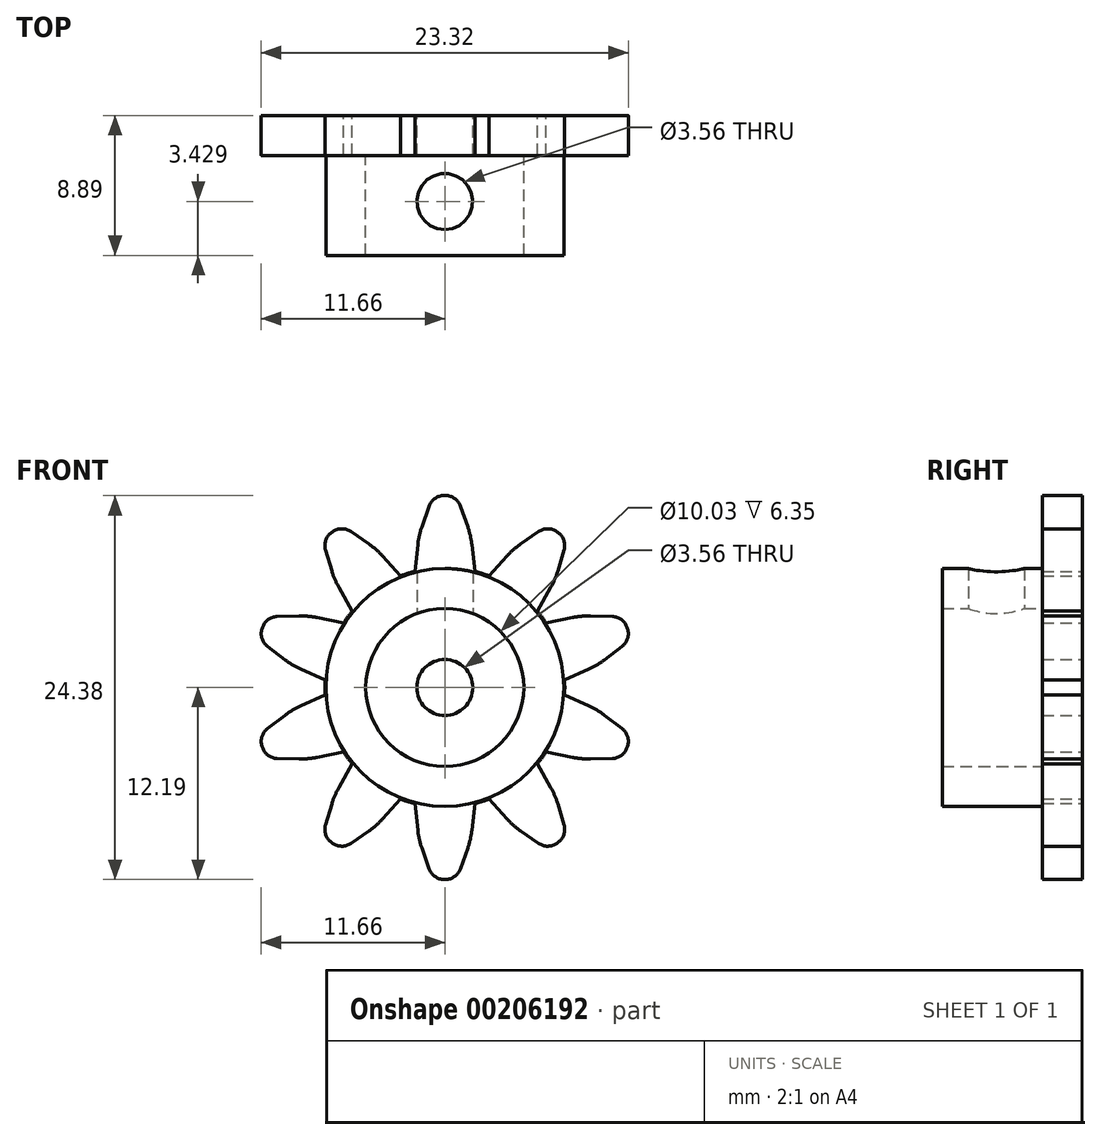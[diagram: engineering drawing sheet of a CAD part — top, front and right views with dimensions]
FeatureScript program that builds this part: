
annotation { "Feature Type Name" : "Feature", "Feature Type Description" : "" }
export const myFeature = defineFeature(function(context is Context, id is Id, definition is map)
    precondition{}
    {
        {
            var Q0;
            Q0=qCreatedBy(makeId("Front.planeOp"),FACE);
            var sketch = newSketch(context, id + "F0", { "sketchPlane" : qUnion([Q0])});
            skCircle(sketch, "E0", {"center": v(0, 0) * mm, "radius": 7.62 * mm});
            skLineSegment(sketch, "E1", {"start": v(-1.9, 7.38) * mm, "end": v(-0.76, 12.2) * mm, "construction": true});
            skLineSegment(sketch, "E2", {"start": v(-0.76, 12.2) * mm, "end": v(0.76, 12.2) * mm});
            skLineSegment(sketch, "E3", {"start": v(0.76, 12.2) * mm, "end": v(1.9, 7.38) * mm, "construction": true});
            skLineSegment(sketch, "E4", {"start": v(-1.9, 7.38) * mm, "end": v(-1.65, 9.65) * mm});
            skPoint(sketch, "E4.endSnap0", {"position": v(-1.33, 9.79) * mm});
            skLineSegment(sketch, "E5", {"start": v(-1.65, 9.65) * mm, "end": v(-0.76, 12.2) * mm});
            skLineSegment(sketch, "E6", {"start": v(1.9, 7.38) * mm, "end": v(1.65, 9.65) * mm});
            skPoint(sketch, "E6.endSnap0", {"position": v(1.33, 9.79) * mm});
            skLineSegment(sketch, "E7", {"start": v(1.65, 9.65) * mm, "end": v(0.76, 12.2) * mm});
            skLineSegment(sketch, "E8.1.0", {"start": v(-7.78, 9.42) * mm, "end": v(-6.55, 10.31) * mm});
            skLineSegment(sketch, "E8.1.1", {"start": v(-4.34, 8.78) * mm, "end": v(-6.55, 10.31) * mm});
            skLineSegment(sketch, "E8.1.2", {"start": v(-2.8, 7.09) * mm, "end": v(-4.34, 8.78) * mm});
            skLineSegment(sketch, "E8.1.3", {"start": v(-7, 6.84) * mm, "end": v(-7.78, 9.42) * mm});
            skLineSegment(sketch, "E8.1.4", {"start": v(-5.88, 4.85) * mm, "end": v(-7, 6.84) * mm});
            skLineSegment(sketch, "E8.2.0", {"start": v(-11.83, 3.04) * mm, "end": v(-11.36, 4.5) * mm});
            skLineSegment(sketch, "E8.2.1", {"start": v(-8.67, 4.55) * mm, "end": v(-11.36, 4.5) * mm});
            skLineSegment(sketch, "E8.2.2", {"start": v(-6.43, 4.1) * mm, "end": v(-8.67, 4.55) * mm});
            skLineSegment(sketch, "E8.2.3", {"start": v(-9.69, 1.41) * mm, "end": v(-11.83, 3.04) * mm});
            skLineSegment(sketch, "E8.2.4", {"start": v(-7.6, 0.47) * mm, "end": v(-9.69, 1.41) * mm});
            skLineSegment(sketch, "E8.3.0", {"start": v(-11.36, -4.5) * mm, "end": v(-11.83, -3.04) * mm});
            skLineSegment(sketch, "E8.3.1", {"start": v(-9.69, -1.41) * mm, "end": v(-11.83, -3.04) * mm});
            skLineSegment(sketch, "E8.3.2", {"start": v(-7.6, -0.47) * mm, "end": v(-9.69, -1.41) * mm});
            skLineSegment(sketch, "E8.3.3", {"start": v(-8.67, -4.55) * mm, "end": v(-11.36, -4.5) * mm});
            skLineSegment(sketch, "E8.3.4", {"start": v(-6.43, -4.1) * mm, "end": v(-8.67, -4.55) * mm});
            skLineSegment(sketch, "E8.4.0", {"start": v(-6.55, -10.31) * mm, "end": v(-7.78, -9.42) * mm});
            skLineSegment(sketch, "E8.4.1", {"start": v(-7, -6.84) * mm, "end": v(-7.78, -9.42) * mm});
            skLineSegment(sketch, "E8.4.2", {"start": v(-5.88, -4.85) * mm, "end": v(-7, -6.84) * mm});
            skLineSegment(sketch, "E8.4.3", {"start": v(-4.34, -8.78) * mm, "end": v(-6.55, -10.31) * mm});
            skLineSegment(sketch, "E8.4.4", {"start": v(-2.8, -7.09) * mm, "end": v(-4.34, -8.78) * mm});
            skLineSegment(sketch, "E8.5.0", {"start": v(0.76, -12.2) * mm, "end": v(-0.76, -12.2) * mm});
            skLineSegment(sketch, "E8.5.1", {"start": v(-1.65, -9.65) * mm, "end": v(-0.76, -12.2) * mm});
            skLineSegment(sketch, "E8.5.2", {"start": v(-1.9, -7.38) * mm, "end": v(-1.65, -9.65) * mm});
            skLineSegment(sketch, "E8.5.3", {"start": v(1.65, -9.65) * mm, "end": v(0.76, -12.2) * mm});
            skLineSegment(sketch, "E8.5.4", {"start": v(1.9, -7.38) * mm, "end": v(1.65, -9.65) * mm});
            skLineSegment(sketch, "E8.6.0", {"start": v(7.78, -9.42) * mm, "end": v(6.55, -10.31) * mm});
            skLineSegment(sketch, "E8.6.1", {"start": v(4.34, -8.78) * mm, "end": v(6.55, -10.31) * mm});
            skLineSegment(sketch, "E8.6.2", {"start": v(2.8, -7.09) * mm, "end": v(4.34, -8.78) * mm});
            skLineSegment(sketch, "E8.6.3", {"start": v(7, -6.84) * mm, "end": v(7.78, -9.42) * mm});
            skLineSegment(sketch, "E8.6.4", {"start": v(5.88, -4.85) * mm, "end": v(7, -6.84) * mm});
            skLineSegment(sketch, "E8.7.0", {"start": v(11.83, -3.04) * mm, "end": v(11.36, -4.5) * mm});
            skLineSegment(sketch, "E8.7.1", {"start": v(8.67, -4.55) * mm, "end": v(11.36, -4.5) * mm});
            skLineSegment(sketch, "E8.7.2", {"start": v(6.43, -4.1) * mm, "end": v(8.67, -4.55) * mm});
            skLineSegment(sketch, "E8.7.3", {"start": v(9.69, -1.41) * mm, "end": v(11.83, -3.04) * mm});
            skLineSegment(sketch, "E8.7.4", {"start": v(7.6, -0.47) * mm, "end": v(9.69, -1.41) * mm});
            skLineSegment(sketch, "E8.8.0", {"start": v(11.36, 4.5) * mm, "end": v(11.83, 3.04) * mm});
            skLineSegment(sketch, "E8.8.1", {"start": v(9.69, 1.41) * mm, "end": v(11.83, 3.04) * mm});
            skLineSegment(sketch, "E8.8.2", {"start": v(7.6, 0.47) * mm, "end": v(9.69, 1.41) * mm});
            skLineSegment(sketch, "E8.8.3", {"start": v(8.67, 4.55) * mm, "end": v(11.36, 4.5) * mm});
            skLineSegment(sketch, "E8.8.4", {"start": v(6.43, 4.1) * mm, "end": v(8.67, 4.55) * mm});
            skLineSegment(sketch, "E8.9.0", {"start": v(6.55, 10.31) * mm, "end": v(7.78, 9.42) * mm});
            skLineSegment(sketch, "E8.9.1", {"start": v(7, 6.84) * mm, "end": v(7.78, 9.42) * mm});
            skLineSegment(sketch, "E8.9.2", {"start": v(5.88, 4.85) * mm, "end": v(7, 6.84) * mm});
            skLineSegment(sketch, "E8.9.3", {"start": v(4.34, 8.78) * mm, "end": v(6.55, 10.31) * mm});
            skLineSegment(sketch, "E8.9.4", {"start": v(2.8, 7.09) * mm, "end": v(4.34, 8.78) * mm});
            skCircle(sketch, "E9", {"center": v(0, 0) * mm, "radius": 1.78 * mm});
            skSolve(sketch);
        }
        {
            var Q0;
            Q0=qSketchRegion(id+"F0",true);
            extrude(context, id + "F1", {"entities" : qUnion([Q0]), "depth" : 2.54 * mm});
        }
        {
            var Q0;
            Q0=makeQuery(id+"F1.opExtrude","CAP_FACE",FACE,{"disambiguationData":[OSD([sQuery(id+"F0.wireOp",EDGE,"E0"),sQuery(id+"F0.wireOp",EDGE,"E2"),sQuery(id+"F0.wireOp",EDGE,"E4"),sQuery(id+"F0.wireOp",EDGE,"E5"),sQuery(id+"F0.wireOp",EDGE,"E6"),sQuery(id+"F0.wireOp",EDGE,"E7"),sQuery(id+"F0.wireOp",EDGE,"E8.1.0"),sQuery(id+"F0.wireOp",EDGE,"E8.1.1"),sQuery(id+"F0.wireOp",EDGE,"E8.1.2"),sQuery(id+"F0.wireOp",EDGE,"E8.1.3"),sQuery(id+"F0.wireOp",EDGE,"E8.1.4"),sQuery(id+"F0.wireOp",EDGE,"E8.2.0"),sQuery(id+"F0.wireOp",EDGE,"E8.2.1"),sQuery(id+"F0.wireOp",EDGE,"E8.2.2"),sQuery(id+"F0.wireOp",EDGE,"E8.2.3"),sQuery(id+"F0.wireOp",EDGE,"E8.2.4"),sQuery(id+"F0.wireOp",EDGE,"E8.3.0"),sQuery(id+"F0.wireOp",EDGE,"E8.3.1"),sQuery(id+"F0.wireOp",EDGE,"E8.3.2"),sQuery(id+"F0.wireOp",EDGE,"E8.3.3"),sQuery(id+"F0.wireOp",EDGE,"E8.3.4"),sQuery(id+"F0.wireOp",EDGE,"E8.4.0"),sQuery(id+"F0.wireOp",EDGE,"E8.4.1"),sQuery(id+"F0.wireOp",EDGE,"E8.4.2"),sQuery(id+"F0.wireOp",EDGE,"E8.4.3"),sQuery(id+"F0.wireOp",EDGE,"E8.4.4"),sQuery(id+"F0.wireOp",EDGE,"E8.5.0"),sQuery(id+"F0.wireOp",EDGE,"E8.5.1"),sQuery(id+"F0.wireOp",EDGE,"E8.5.2"),sQuery(id+"F0.wireOp",EDGE,"E8.5.3"),sQuery(id+"F0.wireOp",EDGE,"E8.5.4"),sQuery(id+"F0.wireOp",EDGE,"E8.6.0"),sQuery(id+"F0.wireOp",EDGE,"E8.6.1"),sQuery(id+"F0.wireOp",EDGE,"E8.6.2"),sQuery(id+"F0.wireOp",EDGE,"E8.6.3"),sQuery(id+"F0.wireOp",EDGE,"E8.6.4"),sQuery(id+"F0.wireOp",EDGE,"E8.7.0"),sQuery(id+"F0.wireOp",EDGE,"E8.7.1"),sQuery(id+"F0.wireOp",EDGE,"E8.7.2"),sQuery(id+"F0.wireOp",EDGE,"E8.7.3"),sQuery(id+"F0.wireOp",EDGE,"E8.7.4"),sQuery(id+"F0.wireOp",EDGE,"E8.8.0"),sQuery(id+"F0.wireOp",EDGE,"E8.8.1"),sQuery(id+"F0.wireOp",EDGE,"E8.8.2"),sQuery(id+"F0.wireOp",EDGE,"E8.8.3"),sQuery(id+"F0.wireOp",EDGE,"E8.8.4"),sQuery(id+"F0.wireOp",EDGE,"E8.9.0"),sQuery(id+"F0.wireOp",EDGE,"E8.9.1"),sQuery(id+"F0.wireOp",EDGE,"E8.9.2"),sQuery(id+"F0.wireOp",EDGE,"E8.9.3"),sQuery(id+"F0.wireOp",EDGE,"E8.9.4"),sQuery(id+"F0.wireOp",EDGE,"E9")])],"isStart":false});
            var sketch = newSketch(context, id + "F2", { "sketchPlane" : qUnion([Q0])});
            skCircle(sketch, "E10", {"center": v(0, 0) * mm, "radius": 7.56 * mm});
            skCircle(sketch, "E11", {"center": v(0, 0) * mm, "radius": 5.02 * mm});
            skSolve(sketch);
        }
        {
            var Q0;
            Q0=qSketchRegion(id+"F2",true);
            extrude(context, id + "F3", {"entities" : qUnion([Q0]), "operationType" : NewBodyOperationType.ADD, "depth" : 6.35 * mm});
        }
        {
            var Q0;
            Q0=makeQuery(id+"F1.opExtrude","SWEPT_EDGE",EDGE,{"disambiguationData":[OSD([sQuery(id+"F0.wireOp",EDGE,"E8.9.1"),sQuery(id+"F0.wireOp",EDGE,"E8.9.2")])]});
            var Q1;
            Q1=makeQuery(id+"F1.opExtrude","SWEPT_EDGE",EDGE,{"disambiguationData":[OSD([sQuery(id+"F0.wireOp",EDGE,"E8.9.3"),sQuery(id+"F0.wireOp",EDGE,"E8.9.4")])]});
            var Q2;
            Q2=makeQuery(id+"F1.opExtrude","SWEPT_EDGE",EDGE,{"disambiguationData":[OSD([sQuery(id+"F0.wireOp",EDGE,"E6"),sQuery(id+"F0.wireOp",EDGE,"E7")])]});
            var Q3;
            Q3=makeQuery(id+"F1.opExtrude","SWEPT_EDGE",EDGE,{"disambiguationData":[OSD([sQuery(id+"F0.wireOp",EDGE,"E8.1.1"),sQuery(id+"F0.wireOp",EDGE,"E8.1.2")])]});
            var Q4;
            Q4=makeQuery(id+"F1.opExtrude","SWEPT_EDGE",EDGE,{"disambiguationData":[OSD([sQuery(id+"F0.wireOp",EDGE,"E8.2.1"),sQuery(id+"F0.wireOp",EDGE,"E8.2.2")])]});
            var Q5;
            Q5=makeQuery(id+"F1.opExtrude","SWEPT_EDGE",EDGE,{"disambiguationData":[OSD([sQuery(id+"F0.wireOp",EDGE,"E8.3.1"),sQuery(id+"F0.wireOp",EDGE,"E8.3.2")])]});
            var Q6;
            Q6=makeQuery(id+"F1.opExtrude","SWEPT_EDGE",EDGE,{"disambiguationData":[OSD([sQuery(id+"F0.wireOp",EDGE,"E8.4.1"),sQuery(id+"F0.wireOp",EDGE,"E8.4.2")])]});
            var Q7;
            Q7=makeQuery(id+"F1.opExtrude","SWEPT_EDGE",EDGE,{"disambiguationData":[OSD([sQuery(id+"F0.wireOp",EDGE,"E8.5.1"),sQuery(id+"F0.wireOp",EDGE,"E8.5.2")])]});
            var Q8;
            Q8=makeQuery(id+"F1.opExtrude","SWEPT_EDGE",EDGE,{"disambiguationData":[OSD([sQuery(id+"F0.wireOp",EDGE,"E8.6.1"),sQuery(id+"F0.wireOp",EDGE,"E8.6.2")])]});
            var Q9;
            Q9=makeQuery(id+"F1.opExtrude","SWEPT_EDGE",EDGE,{"disambiguationData":[OSD([sQuery(id+"F0.wireOp",EDGE,"E8.7.1"),sQuery(id+"F0.wireOp",EDGE,"E8.7.2")])]});
            var Q10;
            Q10=makeQuery(id+"F1.opExtrude","SWEPT_EDGE",EDGE,{"disambiguationData":[OSD([sQuery(id+"F0.wireOp",EDGE,"E8.8.1"),sQuery(id+"F0.wireOp",EDGE,"E8.8.2")])]});
            var Q11;
            Q11=makeQuery(id+"F1.opExtrude","SWEPT_EDGE",EDGE,{"disambiguationData":[OSD([sQuery(id+"F0.wireOp",EDGE,"E8.7.3"),sQuery(id+"F0.wireOp",EDGE,"E8.7.4")])]});
            var Q12;
            Q12=makeQuery(id+"F1.opExtrude","SWEPT_EDGE",EDGE,{"disambiguationData":[OSD([sQuery(id+"F0.wireOp",EDGE,"E8.8.3"),sQuery(id+"F0.wireOp",EDGE,"E8.8.4")])]});
            var Q13;
            Q13=makeQuery(id+"F1.opExtrude","SWEPT_EDGE",EDGE,{"disambiguationData":[OSD([sQuery(id+"F0.wireOp",EDGE,"E4"),sQuery(id+"F0.wireOp",EDGE,"E5")])]});
            var Q14;
            Q14=makeQuery(id+"F1.opExtrude","SWEPT_EDGE",EDGE,{"disambiguationData":[OSD([sQuery(id+"F0.wireOp",EDGE,"E8.1.3"),sQuery(id+"F0.wireOp",EDGE,"E8.1.4")])]});
            var Q15;
            Q15=makeQuery(id+"F1.opExtrude","SWEPT_EDGE",EDGE,{"disambiguationData":[OSD([sQuery(id+"F0.wireOp",EDGE,"E8.2.3"),sQuery(id+"F0.wireOp",EDGE,"E8.2.4")])]});
            var Q16;
            Q16=makeQuery(id+"F1.opExtrude","SWEPT_EDGE",EDGE,{"disambiguationData":[OSD([sQuery(id+"F0.wireOp",EDGE,"E8.3.3"),sQuery(id+"F0.wireOp",EDGE,"E8.3.4")])]});
            var Q17;
            Q17=makeQuery(id+"F1.opExtrude","SWEPT_EDGE",EDGE,{"disambiguationData":[OSD([sQuery(id+"F0.wireOp",EDGE,"E8.4.3"),sQuery(id+"F0.wireOp",EDGE,"E8.4.4")])]});
            var Q18;
            Q18=makeQuery(id+"F1.opExtrude","SWEPT_EDGE",EDGE,{"disambiguationData":[OSD([sQuery(id+"F0.wireOp",EDGE,"E8.5.3"),sQuery(id+"F0.wireOp",EDGE,"E8.5.4")])]});
            var Q19;
            Q19=makeQuery(id+"F1.opExtrude","SWEPT_EDGE",EDGE,{"disambiguationData":[OSD([sQuery(id+"F0.wireOp",EDGE,"E8.6.3"),sQuery(id+"F0.wireOp",EDGE,"E8.6.4")])]});
            fillet(context, id + "F4", {"entities" : qUnion([Q0, Q1, Q2, Q3, Q4, Q5, Q6, Q7, Q8, Q9, Q10, Q11, Q12, Q13, Q14, Q15, Q16, Q17, Q18, Q19]), "radius" : 5.08 * mm, "tangentPropagation" : true, "allowEdgeOverflow" : false});
        }
        {
            var Q0;
            Q0=makeQuery(id+"F1.opExtrude","SWEPT_EDGE",EDGE,{"disambiguationData":[OSD([sQuery(id+"F0.wireOp",EDGE,"E2"),sQuery(id+"F0.wireOp",EDGE,"E7")])]});
            var Q1;
            Q1=makeQuery(id+"F1.opExtrude","SWEPT_EDGE",EDGE,{"disambiguationData":[OSD([sQuery(id+"F0.wireOp",EDGE,"E2"),sQuery(id+"F0.wireOp",EDGE,"E5")])]});
            var Q2;
            Q2=makeQuery(id+"F1.opExtrude","SWEPT_EDGE",EDGE,{"disambiguationData":[OSD([sQuery(id+"F0.wireOp",EDGE,"E8.1.0"),sQuery(id+"F0.wireOp",EDGE,"E8.1.1")])]});
            var Q3;
            Q3=makeQuery(id+"F1.opExtrude","SWEPT_EDGE",EDGE,{"disambiguationData":[OSD([sQuery(id+"F0.wireOp",EDGE,"E8.1.0"),sQuery(id+"F0.wireOp",EDGE,"E8.1.3")])]});
            var Q4;
            Q4=makeQuery(id+"F1.opExtrude","SWEPT_EDGE",EDGE,{"disambiguationData":[OSD([sQuery(id+"F0.wireOp",EDGE,"E8.2.0"),sQuery(id+"F0.wireOp",EDGE,"E8.2.1")])]});
            var Q5;
            Q5=makeQuery(id+"F1.opExtrude","SWEPT_EDGE",EDGE,{"disambiguationData":[OSD([sQuery(id+"F0.wireOp",EDGE,"E8.9.0"),sQuery(id+"F0.wireOp",EDGE,"E8.9.3")])]});
            var Q6;
            Q6=makeQuery(id+"F1.opExtrude","SWEPT_EDGE",EDGE,{"disambiguationData":[OSD([sQuery(id+"F0.wireOp",EDGE,"E8.9.0"),sQuery(id+"F0.wireOp",EDGE,"E8.9.1")])]});
            var Q7;
            Q7=makeQuery(id+"F1.opExtrude","SWEPT_EDGE",EDGE,{"disambiguationData":[OSD([sQuery(id+"F0.wireOp",EDGE,"E8.8.0"),sQuery(id+"F0.wireOp",EDGE,"E8.8.3")])]});
            var Q8;
            Q8=makeQuery(id+"F1.opExtrude","SWEPT_EDGE",EDGE,{"disambiguationData":[OSD([sQuery(id+"F0.wireOp",EDGE,"E8.2.0"),sQuery(id+"F0.wireOp",EDGE,"E8.2.3")])]});
            var Q9;
            Q9=makeQuery(id+"F1.opExtrude","SWEPT_EDGE",EDGE,{"disambiguationData":[OSD([sQuery(id+"F0.wireOp",EDGE,"E8.3.0"),sQuery(id+"F0.wireOp",EDGE,"E8.3.1")])]});
            var Q10;
            Q10=makeQuery(id+"F1.opExtrude","SWEPT_EDGE",EDGE,{"disambiguationData":[OSD([sQuery(id+"F0.wireOp",EDGE,"E8.3.0"),sQuery(id+"F0.wireOp",EDGE,"E8.3.3")])]});
            var Q11;
            Q11=makeQuery(id+"F1.opExtrude","SWEPT_EDGE",EDGE,{"disambiguationData":[OSD([sQuery(id+"F0.wireOp",EDGE,"E8.4.0"),sQuery(id+"F0.wireOp",EDGE,"E8.4.1")])]});
            var Q12;
            Q12=makeQuery(id+"F1.opExtrude","SWEPT_EDGE",EDGE,{"disambiguationData":[OSD([sQuery(id+"F0.wireOp",EDGE,"E8.4.0"),sQuery(id+"F0.wireOp",EDGE,"E8.4.3")])]});
            var Q13;
            Q13=makeQuery(id+"F1.opExtrude","SWEPT_EDGE",EDGE,{"disambiguationData":[OSD([sQuery(id+"F0.wireOp",EDGE,"E8.5.0"),sQuery(id+"F0.wireOp",EDGE,"E8.5.1")])]});
            var Q14;
            Q14=makeQuery(id+"F1.opExtrude","SWEPT_EDGE",EDGE,{"disambiguationData":[OSD([sQuery(id+"F0.wireOp",EDGE,"E8.5.0"),sQuery(id+"F0.wireOp",EDGE,"E8.5.3")])]});
            var Q15;
            Q15=makeQuery(id+"F1.opExtrude","SWEPT_EDGE",EDGE,{"disambiguationData":[OSD([sQuery(id+"F0.wireOp",EDGE,"E8.6.0"),sQuery(id+"F0.wireOp",EDGE,"E8.6.1")])]});
            var Q16;
            Q16=makeQuery(id+"F1.opExtrude","SWEPT_EDGE",EDGE,{"disambiguationData":[OSD([sQuery(id+"F0.wireOp",EDGE,"E8.6.0"),sQuery(id+"F0.wireOp",EDGE,"E8.6.3")])]});
            var Q17;
            Q17=makeQuery(id+"F1.opExtrude","SWEPT_EDGE",EDGE,{"disambiguationData":[OSD([sQuery(id+"F0.wireOp",EDGE,"E8.7.0"),sQuery(id+"F0.wireOp",EDGE,"E8.7.3")])]});
            var Q18;
            Q18=makeQuery(id+"F1.opExtrude","SWEPT_EDGE",EDGE,{"disambiguationData":[OSD([sQuery(id+"F0.wireOp",EDGE,"E8.7.0"),sQuery(id+"F0.wireOp",EDGE,"E8.7.1")])]});
            var Q19;
            Q19=makeQuery(id+"F1.opExtrude","SWEPT_EDGE",EDGE,{"disambiguationData":[OSD([sQuery(id+"F0.wireOp",EDGE,"E8.8.0"),sQuery(id+"F0.wireOp",EDGE,"E8.8.1")])]});
            fillet(context, id + "F5", {"entities" : qUnion([Q0, Q1, Q2, Q3, Q4, Q5, Q6, Q7, Q8, Q9, Q10, Q11, Q12, Q13, Q14, Q15, Q16, Q17, Q18, Q19]), "radius" : 1.02 * mm, "tangentPropagation" : true, "allowEdgeOverflow" : false});
        }
        {
            var Q0;
            Q0=qCreatedBy(makeId("Top.planeOp"),FACE);
            var sketch = newSketch(context, id + "F6", { "sketchPlane" : qUnion([Q0])});
            skCircle(sketch, "E12", {"center": v(0, -5.46) * mm, "radius": 1.78 * mm});
            skSolve(sketch);
        }
        {
            var Q0;
            Q0=qSketchRegion(id+"F6",true);
            extrude(context, id + "F7", {"entities" : qUnion([Q0]), "operationType" : NewBodyOperationType.REMOVE, "depth" : 25.4 * mm});
        }
    });
